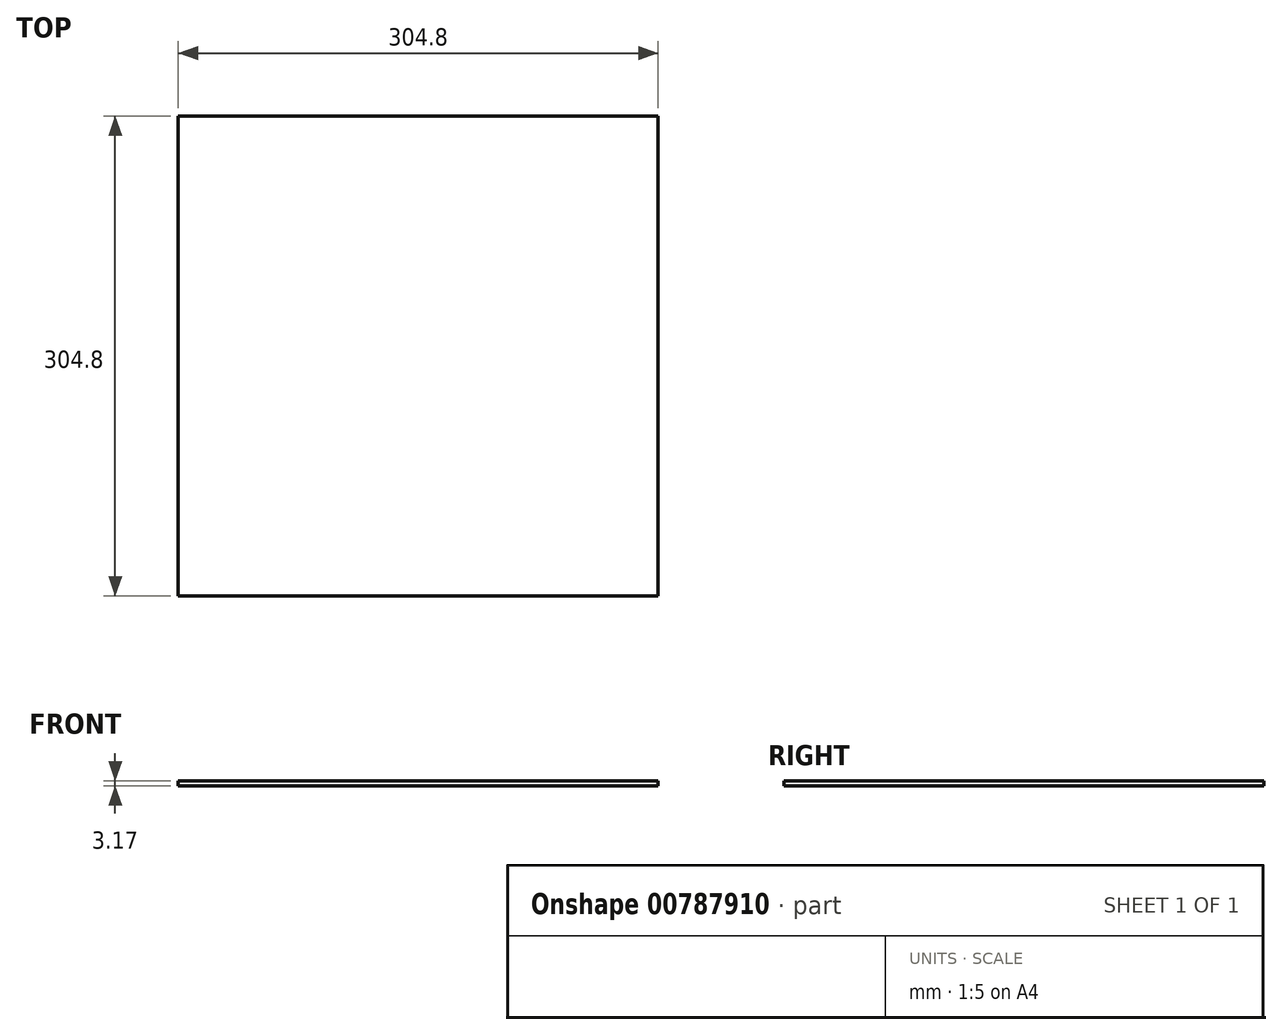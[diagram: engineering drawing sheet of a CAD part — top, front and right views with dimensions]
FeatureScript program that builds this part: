
annotation { "Feature Type Name" : "Feature", "Feature Type Description" : "" }
export const myFeature = defineFeature(function(context is Context, id is Id, definition is map)
    precondition{}
    {
        {
            var Q0;
            Q0=qCreatedBy(makeId("Top.planeOp"),FACE);
            var sketch = newSketch(context, id + "F0", { "sketchPlane" : qUnion([Q0])});
            skLineSegment(sketch, "E0.bottom", {"start": v(184.87, -172.37) * mm, "end": v(-119.93, -172.37) * mm});
            skLineSegment(sketch, "E0.top", {"start": v(184.87, 132.43) * mm, "end": v(-119.93, 132.43) * mm});
            skLineSegment(sketch, "E0.left", {"start": v(184.87, -172.37) * mm, "end": v(184.87, 132.43) * mm});
            skLineSegment(sketch, "E0.right", {"start": v(-119.93, -172.37) * mm, "end": v(-119.93, 132.43) * mm});
            skSolve(sketch);
        }
        {
            var Q0;
            Q0=qSketchRegion(id+"F0",true);
            extrude(context, id + "F1", {"entities" : qUnion([Q0]), "depth" : 3.17 * mm, "offsetDistance" : 25.4 * mm});
        }
    });
